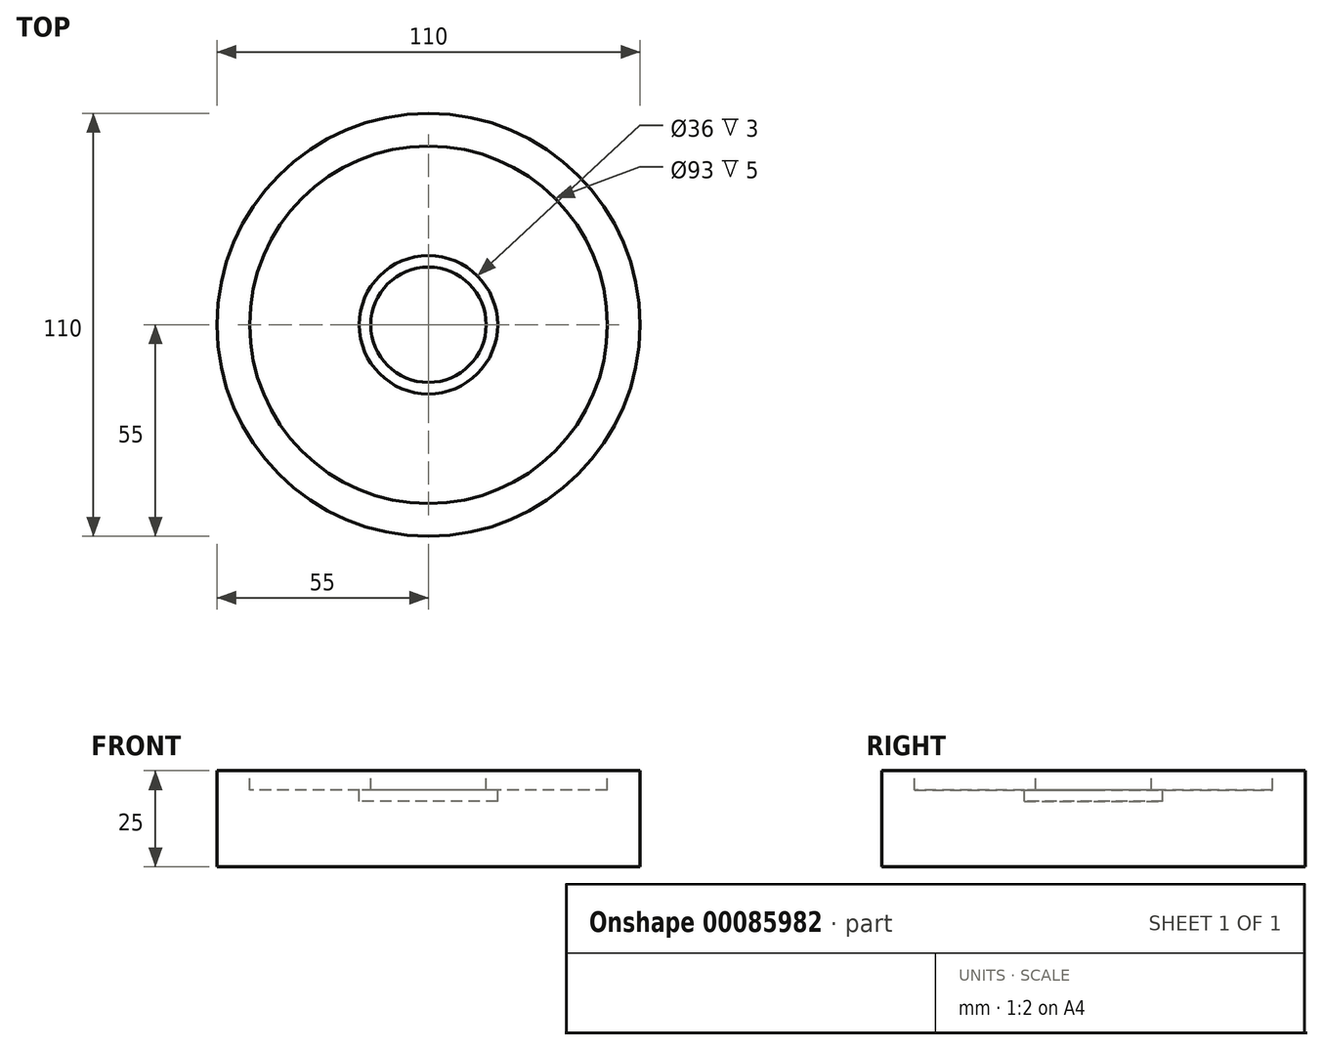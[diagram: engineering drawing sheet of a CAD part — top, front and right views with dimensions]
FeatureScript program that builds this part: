
annotation { "Feature Type Name" : "Feature", "Feature Type Description" : "" }
export const myFeature = defineFeature(function(context is Context, id is Id, definition is map)
    precondition{}
    {
        {
            var Q0;
            Q0=qCreatedBy(makeId("Front.planeOp"),FACE);
            var sketch = newSketch(context, id + "F0", { "sketchPlane" : qUnion([Q0])});
            skLineSegment(sketch, "E0.bottom", {"start": v(55, 12.5) * mm, "end": v(46.5, 12.5) * mm});
            skLineSegment(sketch, "E0.top", {"start": v(55, -12.5) * mm, "end": v(-55, -12.5) * mm});
            skLineSegment(sketch, "E0.left", {"start": v(55, 12.5) * mm, "end": v(55, -12.5) * mm});
            skLineSegment(sketch, "E0.right", {"start": v(-55, 12.5) * mm, "end": v(-55, -12.5) * mm});
            skPoint(sketch, "E0.middle", {"position": v(0, 0) * mm});
            skLineSegment(sketch, "E1.top", {"start": v(46.5, 7.5) * mm, "end": v(18, 7.5) * mm});
            skLineSegment(sketch, "E1.left", {"start": v(46.5, 12.5) * mm, "end": v(46.5, 7.5) * mm});
            skLineSegment(sketch, "E1.right", {"start": v(-46.5, 12.5) * mm, "end": v(-46.5, 7.5) * mm});
            skLineSegment(sketch, "E2.bottom", {"start": v(15, 12.5) * mm, "end": v(-15, 12.5) * mm});
            skLineSegment(sketch, "E2.left", {"start": v(15, 12.5) * mm, "end": v(15, 4.5) * mm});
            skLineSegment(sketch, "E2.right", {"start": v(-15, 12.5) * mm, "end": v(-15, 4.5) * mm});
            skPoint(sketch, "E2.middle", {"position": v(0, 7.5) * mm});
            skLineSegment(sketch, "E3", {"start": v(-15, 4.5) * mm, "end": v(15, 4.5) * mm});
            skLineSegment(sketch, "E4.bottom", {"start": v(-15, 7.5) * mm, "end": v(15, 7.5) * mm});
            skLineSegment(sketch, "E4.left", {"start": v(-18, 7.5) * mm, "end": v(-18, 4.5) * mm});
            skLineSegment(sketch, "E4.right", {"start": v(18, 7.5) * mm, "end": v(18, 4.5) * mm});
            skPoint(sketch, "E4.middle", {"position": v(0, 4.5) * mm});
            skLineSegment(sketch, "E5", {"start": v(15, 4.5) * mm, "end": v(18, 4.5) * mm});
            skLineSegment(sketch, "E6", {"start": v(-18, 4.5) * mm, "end": v(-15, 4.5) * mm});
            skLineSegment(sketch, "E7.trimOffspring", {"start": v(-18, 7.5) * mm, "end": v(-46.5, 7.5) * mm});
            skLineSegment(sketch, "E8.trimOffspring", {"start": v(15, 7.5) * mm, "end": v(-15, 7.5) * mm});
            skLineSegment(sketch, "E9", {"start": v(0, -17.76) * mm, "end": v(0, -17.76) * mm});
            skPoint(sketch, "E9.endSnap0", {"position": v(0, 12.5) * mm});
            skLineSegment(sketch, "E10.trimOffspring", {"start": v(-46.5, 12.5) * mm, "end": v(-55, 12.5) * mm});
            skLineSegment(sketch, "E11", {"start": v(0, 24.26) * mm, "end": v(0, -30.15) * mm});
            skSolve(sketch);
        }
        {
            var Q0;
            {var subQ4=sQuery(id+"F0.wireOp",EDGE,"E0.right");Q0=makeQuery(id+"F0.imprint","IMPRINT",FACE,{"disambiguationData":[TD([[makeQuery(id+"F0.imprint","IMPRINT",EDGE,{"derivedFrom":subQ4}),1.0]])]});}
            var Q1;
            {var subQ1=sQuery(id+"F0.wireOp",EDGE,"E2.right");var subQ3=sQuery(id+"F0.wireOp",EDGE,"E8.trimOffspring");var subQ4=makeQuery(id+"F0.imprint","INTERSECT",VERTEX,{"derivedFrom":[subQ1,subQ3]});Q1=makeQuery(id+"F0.imprint","IMPRINT",FACE,{"disambiguationData":[TD([[makeQuery(id+"F0.imprint","IMPRINT",EDGE,{"disambiguationData":[TD([[subQ4,1.0]])],"derivedFrom":subQ3}),1.0]])]});}
            var Q2;
            {var subQ0=sQuery(id+"F0.wireOp",EDGE,"E2.bottom");var subQ1=sQuery(id+"F0.wireOp",EDGE,"E2.right");var subQ2=makeQuery(id+"F0.imprint","INTERSECT",VERTEX,{"derivedFrom":[subQ1,subQ0]});Q2=makeQuery(id+"F0.imprint","IMPRINT",FACE,{"disambiguationData":[TD([[makeQuery(id+"F0.imprint","IMPRINT",EDGE,{"disambiguationData":[TD([[subQ2,-1.0]])],"derivedFrom":subQ1}),1.0]])]});}
            var Q3;
            Q3=sQuery(id+"F0.wireOp",EDGE,"E11");
            revolve(context, id + "F1", {"entities" : qUnion([Q0, Q1, Q2]), "axis" : qUnion([Q3]), "revolveType" : RevolveType.FULL});
        }
    });
